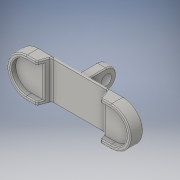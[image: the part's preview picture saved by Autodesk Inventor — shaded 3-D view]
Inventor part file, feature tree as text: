
AUTODESK INVENTOR PART (.ipt)
format: ipt  version: 2016 (Build 200138000, 138)  size: 440,832 bytes
history: native  units: in
note: dims shown in document units (in); Inventor stores cm internally (conversion verified against a paired STEP export)
features: fillet x8, extrude x6, sketch x6, chamfer x1
ambient origin geometry x8: Origin, YZ Plane, XZ Plane, XY Plane, X Axis, Y Axis, Z Axis, Center Point
bodies: Solid1 (feature_tree)
feature tree (21):
  extrude  "Extrusion1"  Depth=0.75in
  fillet  "Fillet1"  Radius=0.25in
  extrude  "Extrusion2"  Depth=2.9in
  extrude  "Extrusion3"  Depth=1.325in
  extrude  "Extrusion4"  Depth=0.39in
  fillet  "Fillet2"  Radius=0.2in
  fillet  "Fillet3"  [1 undecoded]
  extrude  "Extrusion5"  Depth=0.1in
  fillet  "Fillet5"  Radius=0.1in
  fillet  "Fillet6"  Radius=0.325in
  extrude  "Extrusion6"  Depth=0.05in
  fillet  "Fillet7"  Radius=0.7in
  chamfer  "Chamfer1"  Distance=0.275in
  fillet  "Fillet8"  [1 undecoded]
  fillet  "Fillet9"  Radius=0.1in
  sketch  "Sketch1"  dims[d0=0.5in d1=0.75in d2=0.25in d3=0.0in]
  sketch  "Sketch2"  dims[d4=0.25in d5=2.9in]
  sketch  "Sketch3"  dims[d6=0.78in d7=1.325in]
  sketch  "Sketch4"  dims[d8=0.0in d9=0.39in d10=0.2in d11=0.0in d12=0.0in]
  sketch  "Sketch5"  dims[d13=0.0in d14=0.39in d15=0.1in d16=0.325in d17=0.0in]
  sketch  "Sketch6"  dims[d19=0.125in d20=1.4in d21=0.7in d22=0.275in d23=0.0in d24=0.1in d25=1.0in d26=0.0in d27=0.05in d28=0.025in d30=0.25in d31=1.0in d32=0.0in d33=0.025in d34=0.025in d36=0.415in d37=0.15in d38=0.75in d39=1.0in d40=0.0in d41=0.0in d42=0.05in d43=0.2in d44=0.1in d45=0.125in d46=45.0deg d47=0.05in d48=0.05in]
note: 2 required parameter values undecoded (feature->parameter linkage not recoverable at this tier; creation-order binding heuristic only, values carry confidence <= 0.55)
